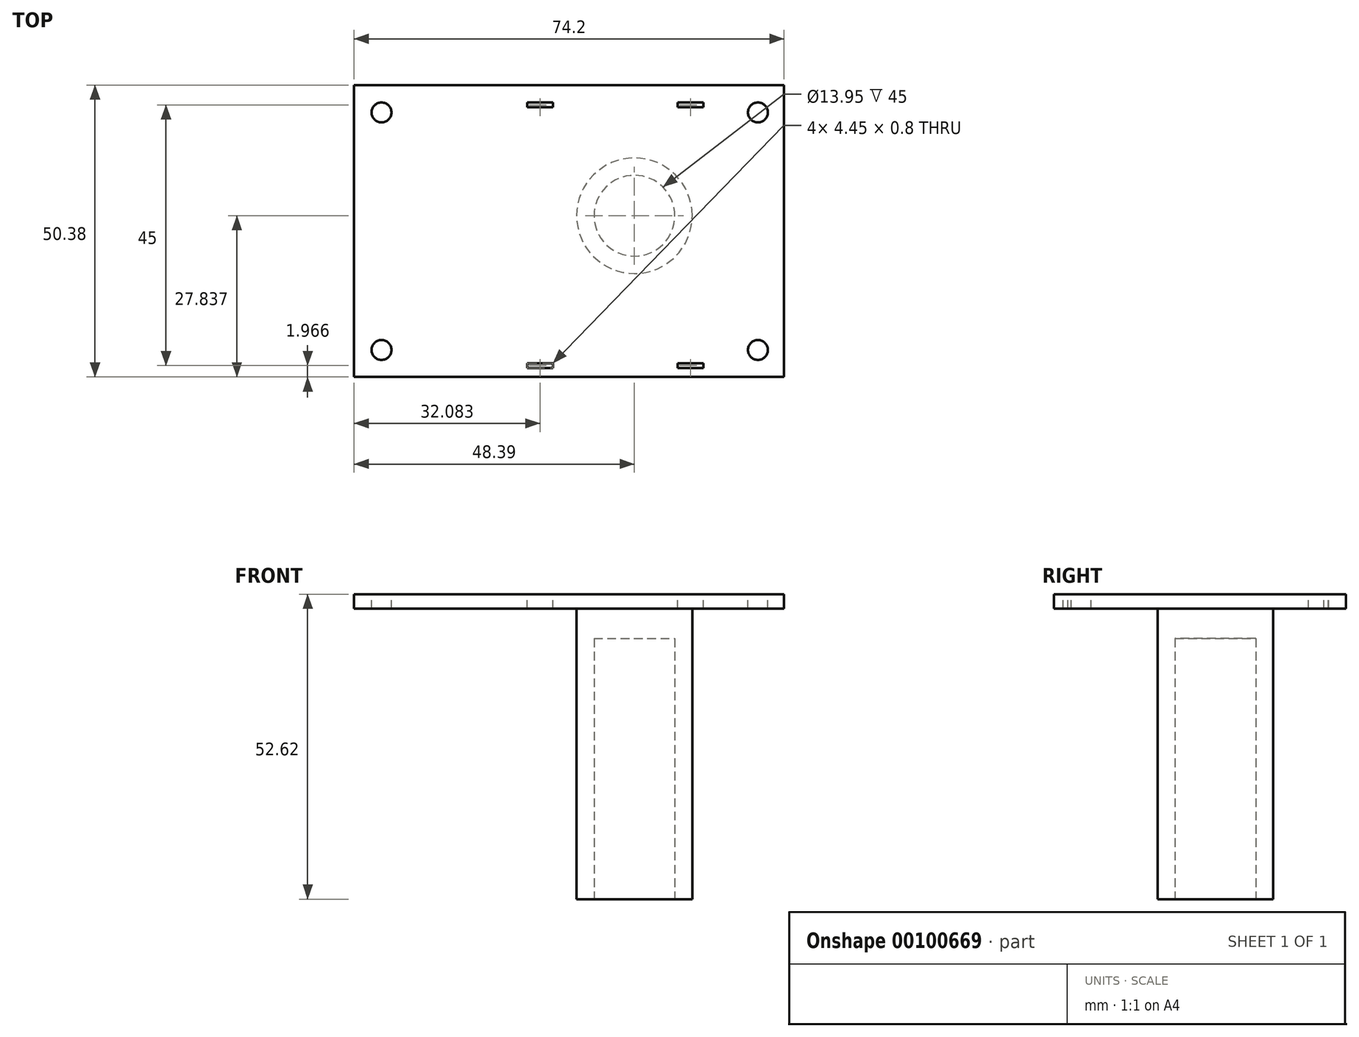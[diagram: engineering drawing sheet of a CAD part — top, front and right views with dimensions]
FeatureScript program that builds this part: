
annotation { "Feature Type Name" : "Feature", "Feature Type Description" : "" }
export const myFeature = defineFeature(function(context is Context, id is Id, definition is map)
    precondition{}
    {
        {
            var Q0;
            Q0=qCreatedBy(makeId("Top.planeOp"),FACE);
            var sketch = newSketch(context, id + "F0", { "sketchPlane" : qUnion([Q0])});
            skLineSegment(sketch, "E0.bottom", {"start": v(-48.4, 37.1) * mm, "end": v(50.89, 37.1) * mm});
            skLineSegment(sketch, "E0.top", {"start": v(-48.4, -62.18) * mm, "end": v(50.89, -62.18) * mm});
            skLineSegment(sketch, "E0.left", {"start": v(-48.4, 37.1) * mm, "end": v(-48.4, -62.18) * mm});
            skLineSegment(sketch, "E0.right", {"start": v(50.89, 37.1) * mm, "end": v(50.89, -62.18) * mm});
            skSolve(sketch);
        }
        {
            var Q0;
            Q0=qSketchRegion(id+"F0",true);
            extrude(context, id + "F1", {"entities" : qUnion([Q0]), "depth" : 5 * mm});
        }
        {
            var Q0;
            Q0=makeQuery(id+"F1.opExtrude","CAP_FACE",FACE,{"disambiguationData":[OSD([sQuery(id+"F0.wireOp",EDGE,"E0.bottom"),sQuery(id+"F0.wireOp",EDGE,"E0.top"),sQuery(id+"F0.wireOp",EDGE,"E0.left"),sQuery(id+"F0.wireOp",EDGE,"E0.right")])],"isStart":true});
            var sketch = newSketch(context, id + "F2", { "sketchPlane" : qUnion([Q0])});
            skCircle(sketch, "E1", {"center": v(0, 12.2) * mm, "radius": 9.97 * mm});
            skSolve(sketch);
        }
        {
            var Q0;
            Q0=qSketchRegion(id+"F2",true);
            extrude(context, id + "F3", {"entities" : qUnion([Q0]), "operationType" : NewBodyOperationType.ADD, "depth" : 50.12 * mm});
        }
        {
            var Q0;
            Q0=makeQuery(id+"F3.opExtrude","CAP_FACE",FACE,{"disambiguationData":[OSD([sQuery(id+"F2.wireOp",EDGE,"E1")])],"isStart":false});
            var sketch = newSketch(context, id + "F4", { "sketchPlane" : qUnion([Q0])});
            skCircle(sketch, "E2", {"center": v(0, 12.2) * mm, "radius": 6.97 * mm});
            skSolve(sketch);
        }
        {
            var Q0;
            Q0=qSketchRegion(id+"F4",true);
            extrude(context, id + "F5", {"entities" : qUnion([Q0]), "operationType" : NewBodyOperationType.REMOVE, "oppositeDirection" : true, "depth" : 45 * mm});
        }
        {
            var Q0;
            Q0=makeQuery(id+"F1.opExtrude","CAP_FACE",FACE,{"disambiguationData":[OSD([sQuery(id+"F0.wireOp",EDGE,"E0.bottom"),sQuery(id+"F0.wireOp",EDGE,"E0.top"),sQuery(id+"F0.wireOp",EDGE,"E0.left"),sQuery(id+"F0.wireOp",EDGE,"E0.right")])],"isStart":false});
            var sketch = newSketch(context, id + "F6", { "sketchPlane" : qUnion([Q0])});
            skLineSegment(sketch, "E3.bottom", {"start": v(-28.44, 4.21) * mm, "end": v(-18.3, 4.21) * mm});
            skLineSegment(sketch, "E3.top", {"start": v(-28.44, -29.14) * mm, "end": v(-18.3, -29.14) * mm});
            skLineSegment(sketch, "E3.left", {"start": v(-28.44, 4.21) * mm, "end": v(-28.44, -29.14) * mm});
            skLineSegment(sketch, "E3.right", {"start": v(-18.3, 4.21) * mm, "end": v(-18.3, -29.14) * mm});
            skSolve(sketch);
        }
        {
            var Q0;
            Q0=qSketchRegion(id+"F6",true);
            extrude(context, id + "F7", {"entities" : qUnion([Q0]), "operationType" : NewBodyOperationType.ADD, "depth" : 51.54 * mm});
        }
        {
            var Q0;
            Q0=makeQuery(id+"F7.opExtrude","SWEPT_FACE",FACE,{"disambiguationData":[OSD([sQuery(id+"F6.wireOp",EDGE,"E3.right")])]});
            var sketch = newSketch(context, id + "F8", { "sketchPlane" : qUnion([Q0])});
            skLineSegment(sketch, "E4.bottom", {"start": v(-22.44, 56.54) * mm, "end": v(-2.6, 56.54) * mm});
            skLineSegment(sketch, "E4.top", {"start": v(-22.44, 39.28) * mm, "end": v(-2.6, 39.28) * mm});
            skLineSegment(sketch, "E4.left", {"start": v(-22.44, 56.54) * mm, "end": v(-22.44, 39.28) * mm});
            skLineSegment(sketch, "E4.right", {"start": v(-2.6, 56.54) * mm, "end": v(-2.6, 39.28) * mm});
            skSolve(sketch);
        }
        {
            var Q0;
            Q0=qSketchRegion(id+"F8",true);
            extrude(context, id + "F9", {"entities" : qUnion([Q0]), "operationType" : NewBodyOperationType.REMOVE, "endBound" : BoundingType.THROUGH_ALL, "oppositeDirection" : true, "depth" : 25 * mm});
        }
        {
            var Q0;
            Q0=makeQuery(id+"F7.opExtrude","SWEPT_FACE",FACE,{"disambiguationData":[OSD([sQuery(id+"F6.wireOp",EDGE,"E3.right")])]});
            var sketch = newSketch(context, id + "F10", { "sketchPlane" : qUnion([Q0])});
            skCircle(sketch, "E5", {"center": v(-25.66, 52.12) * mm, "radius": 1.72 * mm});
            skCircle(sketch, "E6.0.1.0", {"center": v(-25.66, 47.2) * mm, "radius": 1.72 * mm});
            skLineSegment(sketch, "E6.direction1", {"start": v(-25.66, 52.12) * mm, "end": v(-0.66, 52.12) * mm, "construction": true});
            skLineSegment(sketch, "E6.direction2", {"start": v(-25.66, 52.12) * mm, "end": v(-25.66, 47.2) * mm, "construction": true});
            skSolve(sketch);
        }
        {
            var Q0;
            Q0=qSketchRegion(id+"F10",true);
            extrude(context, id + "F11", {"entities" : qUnion([Q0]), "operationType" : NewBodyOperationType.REMOVE, "endBound" : BoundingType.THROUGH_ALL, "oppositeDirection" : true, "depth" : 25 * mm});
        }
        {
            var Q0;
            Q0=makeQuery(id+"F1.opExtrude","CAP_FACE",FACE,{"disambiguationData":[OSD([sQuery(id+"F0.wireOp",EDGE,"E0.bottom"),sQuery(id+"F0.wireOp",EDGE,"E0.top"),sQuery(id+"F0.wireOp",EDGE,"E0.left"),sQuery(id+"F0.wireOp",EDGE,"E0.right")])],"isStart":false});
            var sketch = newSketch(context, id + "F12", { "sketchPlane" : qUnion([Q0])});
            skLineSegment(sketch, "E7.bottom", {"start": v(-48.4, 37.1) * mm, "end": v(50.89, 37.1) * mm});
            skLineSegment(sketch, "E7.top", {"start": v(-48.4, 10.34) * mm, "end": v(50.89, 10.34) * mm});
            skLineSegment(sketch, "E7.left", {"start": v(-48.4, 37.1) * mm, "end": v(-48.4, 10.34) * mm});
            skLineSegment(sketch, "E7.right", {"start": v(50.89, 37.1) * mm, "end": v(50.89, 10.34) * mm});
            skSolve(sketch);
        }
        {
            var Q0;
            Q0=qSketchRegion(id+"F12",true);
            extrude(context, id + "F13", {"entities" : qUnion([Q0]), "operationType" : NewBodyOperationType.REMOVE, "endBound" : BoundingType.THROUGH_ALL, "oppositeDirection" : true, "depth" : 25 * mm});
        }
        {
            var Q0;
            Q0=makeQuery(id+"F1.opExtrude","CAP_FACE",FACE,{"disambiguationData":[OSD([sQuery(id+"F0.wireOp",EDGE,"E0.bottom"),sQuery(id+"F0.wireOp",EDGE,"E0.top"),sQuery(id+"F0.wireOp",EDGE,"E0.left"),sQuery(id+"F0.wireOp",EDGE,"E0.right")])],"isStart":false});
            var sketch = newSketch(context, id + "F14", { "sketchPlane" : qUnion([Q0])});
            skLineSegment(sketch, "E8.bottom", {"start": v(25.8, 10.34) * mm, "end": v(50.89, 10.34) * mm});
            skLineSegment(sketch, "E8.top", {"start": v(25.8, -62.18) * mm, "end": v(50.89, -62.18) * mm});
            skLineSegment(sketch, "E8.left", {"start": v(25.8, 10.34) * mm, "end": v(25.8, -62.18) * mm});
            skLineSegment(sketch, "E8.right", {"start": v(50.89, 10.34) * mm, "end": v(50.89, -62.18) * mm});
            skSolve(sketch);
        }
        {
            var Q0;
            Q0=qSketchRegion(id+"F14",true);
            extrude(context, id + "F15", {"entities" : qUnion([Q0]), "operationType" : NewBodyOperationType.REMOVE, "endBound" : BoundingType.THROUGH_ALL, "oppositeDirection" : true, "depth" : 25 * mm});
        }
        {
            var Q0;
            Q0=makeQuery(id+"F1.opExtrude","CAP_FACE",FACE,{"disambiguationData":[OSD([sQuery(id+"F0.wireOp",EDGE,"E0.bottom"),sQuery(id+"F0.wireOp",EDGE,"E0.top"),sQuery(id+"F0.wireOp",EDGE,"E0.left"),sQuery(id+"F0.wireOp",EDGE,"E0.right")])],"isStart":false});
            var sketch = newSketch(context, id + "F16", { "sketchPlane" : qUnion([Q0])});
            skLineSegment(sketch, "E9.bottom", {"start": v(-48.4, -40.04) * mm, "end": v(25.8, -40.04) * mm});
            skLineSegment(sketch, "E9.top", {"start": v(-48.4, -62.18) * mm, "end": v(25.8, -62.18) * mm});
            skLineSegment(sketch, "E9.left", {"start": v(-48.4, -40.04) * mm, "end": v(-48.4, -62.18) * mm});
            skLineSegment(sketch, "E9.right", {"start": v(25.8, -40.04) * mm, "end": v(25.8, -62.18) * mm});
            skSolve(sketch);
        }
        {
            var Q0;
            Q0=qSketchRegion(id+"F16",true);
            extrude(context, id + "F17", {"entities" : qUnion([Q0]), "operationType" : NewBodyOperationType.REMOVE, "endBound" : BoundingType.THROUGH_ALL, "oppositeDirection" : true, "depth" : 25 * mm});
        }
        {
            var Q0;
            Q0=makeQuery(id+"F7.opExtrude","SWEPT_FACE",FACE,{"disambiguationData":[OSD([sQuery(id+"F6.wireOp",EDGE,"E3.right")])]});
            var sketch = newSketch(context, id + "F18", { "sketchPlane" : qUnion([Q0])});
            skCircle(sketch, "E10", {"center": v(0.74, 52.12) * mm, "radius": 1.72 * mm});
            skCircle(sketch, "E11.0.1.0", {"center": v(0.74, 47.2) * mm, "radius": 1.72 * mm});
            skLineSegment(sketch, "E11.direction1", {"start": v(0.74, 52.12) * mm, "end": v(-24.26, 52.12) * mm, "construction": true});
            skLineSegment(sketch, "E11.direction2", {"start": v(0.74, 52.12) * mm, "end": v(0.74, 47.2) * mm, "construction": true});
            skSolve(sketch);
        }
        {
            var Q0;
            Q0=qSketchRegion(id+"F18",true);
            extrude(context, id + "F19", {"entities" : qUnion([Q0]), "operationType" : NewBodyOperationType.REMOVE, "endBound" : BoundingType.THROUGH_ALL, "oppositeDirection" : true, "depth" : 25 * mm});
        }
        {
            var Q0;
            Q0=makeQuery(id+"F1.opExtrude","CAP_FACE",FACE,{"disambiguationData":[OSD([sQuery(id+"F0.wireOp",EDGE,"E0.bottom"),sQuery(id+"F0.wireOp",EDGE,"E0.top"),sQuery(id+"F0.wireOp",EDGE,"E0.left"),sQuery(id+"F0.wireOp",EDGE,"E0.right")])],"isStart":false});
            var sketch = newSketch(context, id + "F20", { "sketchPlane" : qUnion([Q0])});
            skLineSegment(sketch, "E12.bottom", {"start": v(-18.53, -38.47) * mm, "end": v(-14.08, -38.47) * mm});
            skLineSegment(sketch, "E12.top", {"start": v(-18.53, -37.67) * mm, "end": v(-14.08, -37.67) * mm});
            skLineSegment(sketch, "E12.left", {"start": v(-18.53, -38.47) * mm, "end": v(-18.53, -37.67) * mm});
            skLineSegment(sketch, "E12.right", {"start": v(-14.08, -38.47) * mm, "end": v(-14.08, -37.67) * mm});
            skLineSegment(sketch, "E13.0.1.0", {"start": v(-18.53, 7.33) * mm, "end": v(-14.08, 7.33) * mm});
            skLineSegment(sketch, "E13.0.1.1", {"start": v(-14.08, 6.53) * mm, "end": v(-14.08, 7.33) * mm});
            skLineSegment(sketch, "E13.0.1.2", {"start": v(-18.53, 6.53) * mm, "end": v(-14.08, 6.53) * mm});
            skLineSegment(sketch, "E13.0.1.3", {"start": v(-18.53, 6.53) * mm, "end": v(-18.53, 7.33) * mm});
            skLineSegment(sketch, "E13.1.0.0", {"start": v(7.47, -37.67) * mm, "end": v(11.92, -37.67) * mm});
            skLineSegment(sketch, "E13.1.0.1", {"start": v(11.92, -38.47) * mm, "end": v(11.92, -37.67) * mm});
            skLineSegment(sketch, "E13.1.0.2", {"start": v(7.47, -38.47) * mm, "end": v(11.92, -38.47) * mm});
            skLineSegment(sketch, "E13.1.0.3", {"start": v(7.47, -38.47) * mm, "end": v(7.47, -37.67) * mm});
            skLineSegment(sketch, "E13.1.1.0", {"start": v(7.47, 7.33) * mm, "end": v(11.92, 7.33) * mm});
            skLineSegment(sketch, "E13.1.1.1", {"start": v(11.92, 6.53) * mm, "end": v(11.92, 7.33) * mm});
            skLineSegment(sketch, "E13.1.1.2", {"start": v(7.47, 6.53) * mm, "end": v(11.92, 6.53) * mm});
            skLineSegment(sketch, "E13.1.1.3", {"start": v(7.47, 6.53) * mm, "end": v(7.47, 7.33) * mm});
            skLineSegment(sketch, "E13.direction1", {"start": v(-18.53, -37.67) * mm, "end": v(7.47, -37.67) * mm, "construction": true});
            skLineSegment(sketch, "E13.direction2", {"start": v(-18.53, -37.67) * mm, "end": v(-18.53, 7.33) * mm, "construction": true});
            skSolve(sketch);
        }
        {
            var Q0;
            Q0=qSketchRegion(id+"F20",true);
            extrude(context, id + "F21", {"entities" : qUnion([Q0]), "operationType" : NewBodyOperationType.REMOVE, "endBound" : BoundingType.THROUGH_ALL, "oppositeDirection" : true, "depth" : 25 * mm});
        }
        {
            var Q0;
            Q0=makeQuery(id+"F1.opExtrude","CAP_FACE",FACE,{"disambiguationData":[OSD([sQuery(id+"F0.wireOp",EDGE,"E0.bottom"),sQuery(id+"F0.wireOp",EDGE,"E0.top"),sQuery(id+"F0.wireOp",EDGE,"E0.left"),sQuery(id+"F0.wireOp",EDGE,"E0.right")])],"isStart":false});
            var sketch = newSketch(context, id + "F22", { "sketchPlane" : qUnion([Q0])});
            skCircle(sketch, "E14", {"center": v(-43.67, 5.62) * mm, "radius": 1.72 * mm});
            skCircle(sketch, "E15.0.1.0", {"center": v(-43.67, -35.38) * mm, "radius": 1.72 * mm});
            skCircle(sketch, "E15.1.0.0", {"center": v(21.33, 5.62) * mm, "radius": 1.72 * mm});
            skCircle(sketch, "E15.1.1.0", {"center": v(21.33, -35.38) * mm, "radius": 1.72 * mm});
            skLineSegment(sketch, "E15.direction1", {"start": v(-43.67, 5.62) * mm, "end": v(21.33, 5.62) * mm, "construction": true});
            skLineSegment(sketch, "E15.direction2", {"start": v(-43.67, 5.62) * mm, "end": v(-43.67, -35.38) * mm, "construction": true});
            skSolve(sketch);
        }
        {
            var Q0;
            Q0=qSketchRegion(id+"F22",true);
            extrude(context, id + "F23", {"entities" : qUnion([Q0]), "operationType" : NewBodyOperationType.REMOVE, "endBound" : BoundingType.THROUGH_ALL, "oppositeDirection" : true, "depth" : 25 * mm});
        }
        {
            var Q0;
            Q0=makeQuery(id+"F15.boolean.opBoolean","COPY",FACE,{"derivedFrom":makeQuery(id+"F15.opExtrude","SWEPT_FACE",FACE,{"disambiguationData":[OSD([sQuery(id+"F14.wireOp",EDGE,"E8.left")])]})});
            var sketch = newSketch(context, id + "F24", { "sketchPlane" : qUnion([Q0])});
            skLineSegment(sketch, "E16.bottom", {"start": v(-40.04, 2.5) * mm, "end": v(12.2, 2.5) * mm});
            skLineSegment(sketch, "E16.top", {"start": v(-40.04, 60.93) * mm, "end": v(12.2, 60.93) * mm});
            skLineSegment(sketch, "E16.left", {"start": v(-40.04, 2.5) * mm, "end": v(-40.04, 60.93) * mm});
            skLineSegment(sketch, "E16.right", {"start": v(12.2, 2.5) * mm, "end": v(12.2, 60.93) * mm});
            skSolve(sketch);
        }
        {
            var Q0;
            Q0 = qSketchRegion(id + "F24", true);
            extrude(context, id + "F25", {"entities" : qUnion([Q0]), "operationType" : NewBodyOperationType.REMOVE, "endBound" : BoundingType.THROUGH_ALL, "oppositeDirection" : true, "depth" : 25 * mm});
        }
    });
